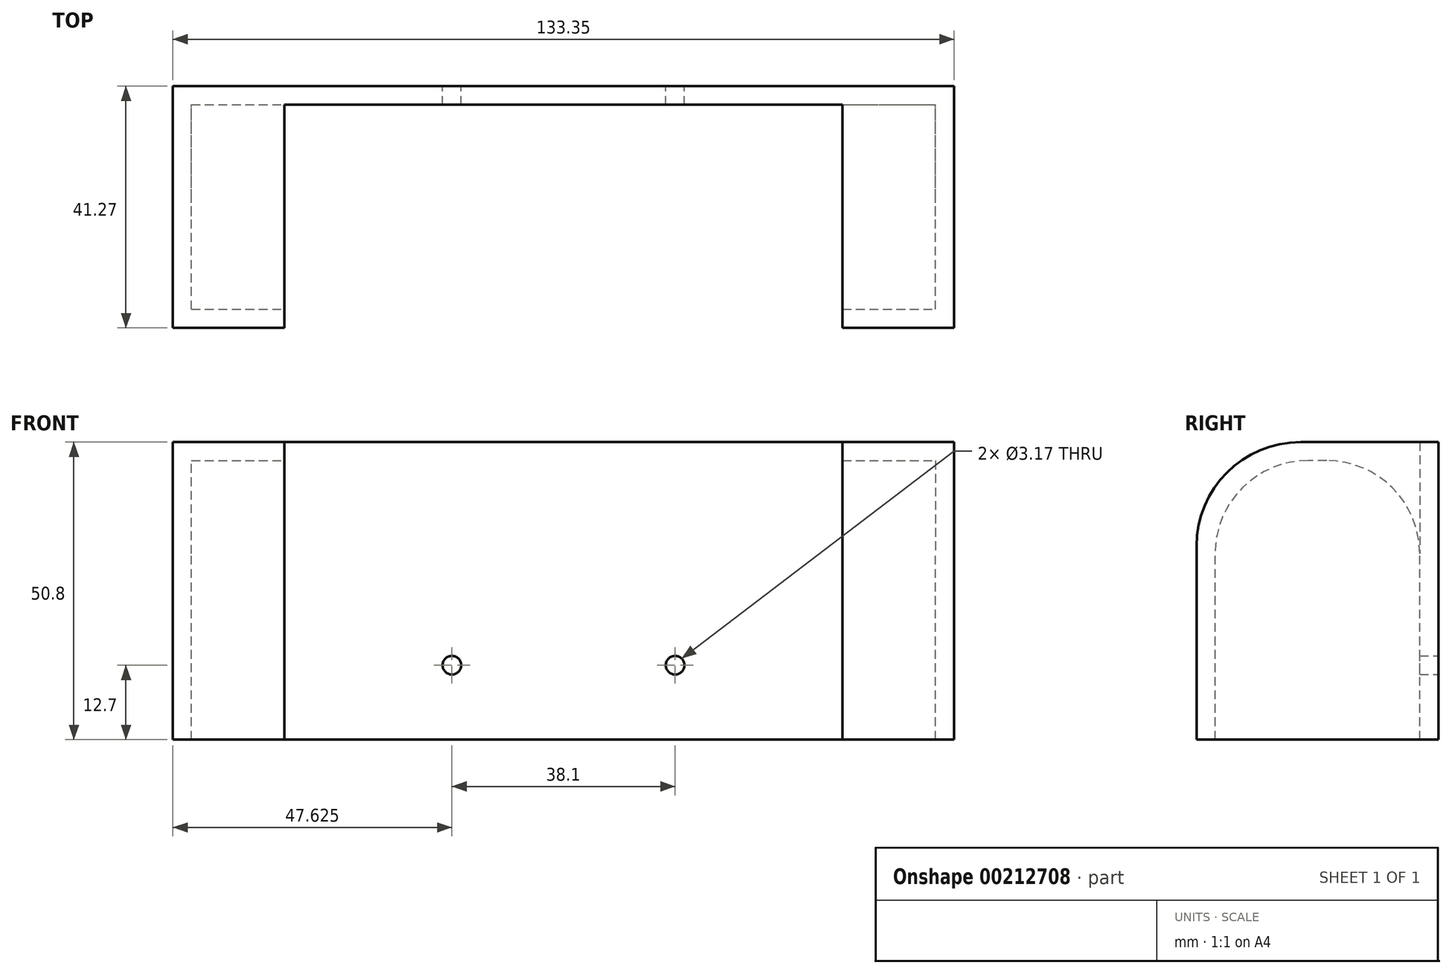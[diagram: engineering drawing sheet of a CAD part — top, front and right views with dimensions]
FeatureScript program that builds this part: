
annotation { "Feature Type Name" : "Feature", "Feature Type Description" : "" }
export const myFeature = defineFeature(function(context is Context, id is Id, definition is map)
    precondition{}
    {
        {
            var Q0;
            Q0=qCreatedBy(makeId("Front.planeOp"),FACE);
            var sketch = newSketch(context, id + "F0", { "sketchPlane" : qUnion([Q0])});
            skLineSegment(sketch, "E0.bottom", {"start": v(0, 0) * mm, "end": v(133.35, 0) * mm});
            skLineSegment(sketch, "E0.top", {"start": v(0, 50.8) * mm, "end": v(133.35, 50.8) * mm});
            skLineSegment(sketch, "E0.left", {"start": v(0, 0) * mm, "end": v(0, 50.8) * mm});
            skLineSegment(sketch, "E0.right", {"start": v(133.35, 0) * mm, "end": v(133.35, 50.8) * mm});
            skSolve(sketch);
        }
        {
            var Q0;
            Q0 = qSketchRegion(id + "F0", true);
            extrude(context, id + "F1", {"entities" : qUnion([Q0]), "depth" : 3.17 * mm});
        }
        {
            var Q0;
            Q0=makeQuery(id+"F1.opExtrude","CAP_FACE",FACE,{"disambiguationData":[OSD([sQuery(id+"F0.wireOp",EDGE,"E0.bottom"),sQuery(id+"F0.wireOp",EDGE,"E0.top"),sQuery(id+"F0.wireOp",EDGE,"E0.left"),sQuery(id+"F0.wireOp",EDGE,"E0.right")])],"isStart":false});
            var sketch = newSketch(context, id + "F2", { "sketchPlane" : qUnion([Q0])});
            skLineSegment(sketch, "E1.bottom", {"start": v(0, 50.8) * mm, "end": v(19.05, 50.8) * mm});
            skLineSegment(sketch, "E1.top", {"start": v(0, 0) * mm, "end": v(19.05, 0) * mm});
            skLineSegment(sketch, "E1.left", {"start": v(0, 50.8) * mm, "end": v(0, 0) * mm});
            skLineSegment(sketch, "E1.right", {"start": v(19.05, 50.8) * mm, "end": v(19.05, 0) * mm});
            skLineSegment(sketch, "E2.bottom", {"start": v(133.35, 50.8) * mm, "end": v(114.3, 50.8) * mm});
            skLineSegment(sketch, "E2.top", {"start": v(133.35, 0) * mm, "end": v(114.3, 0) * mm});
            skLineSegment(sketch, "E2.left", {"start": v(133.35, 50.8) * mm, "end": v(133.35, 0) * mm});
            skLineSegment(sketch, "E2.right", {"start": v(114.3, 50.8) * mm, "end": v(114.3, 0) * mm});
            skSolve(sketch);
        }
        {
            var Q0;
            Q0 = qSketchRegion(id + "F2", true);
            extrude(context, id + "F3", {"entities" : qUnion([Q0]), "operationType" : NewBodyOperationType.ADD, "depth" : 38.1 * mm});
        }
        {
            var Q0;
            Q0=makeQuery(id+"F3.boolean.opBoolean","MERGE",FACE,{"derivedFrom":[makeQuery(id+"F1.opExtrude","SWEPT_FACE",FACE,{"disambiguationData":[OSD([sQuery(id+"F0.wireOp",EDGE,"E0.bottom")])]}),makeQuery(id+"F3.opExtrude","SWEPT_FACE",FACE,{"disambiguationData":[OSD([sQuery(id+"F2.wireOp",EDGE,"E1.top")])]}),makeQuery(id+"F3.opExtrude","SWEPT_FACE",FACE,{"disambiguationData":[OSD([sQuery(id+"F2.wireOp",EDGE,"E2.top")])]})]});
            shell(context, id + "F4", {"entities" : qUnion([Q0]), "thickness" : 3.17 * mm});
        }
        {
            var Q0;
            Q0=makeQuery(id+"F4.opShell","OFFSET_EDGE",EDGE,{"disambiguationData":[OSD([sQuery(id+"F0.wireOp",EDGE,"E0.top")]),OD(0.0)]});
            var Q1;
            Q1=makeQuery(id+"F4.opShell","OFFSET_EDGE",EDGE,{"disambiguationData":[OSD([sQuery(id+"F2.wireOp",EDGE,"E1.bottom")])]});
            var Q2;
            Q2=makeQuery(id+"F4.opShell","OFFSET_EDGE",EDGE,{"disambiguationData":[OSD([sQuery(id+"F2.wireOp",EDGE,"E2.bottom")])]});
            var Q3;
            Q3=makeQuery(id+"F4.opShell","OFFSET_EDGE",EDGE,{"disambiguationData":[OSD([sQuery(id+"F0.wireOp",EDGE,"E0.top")]),OD(1.0)]});
            fillet(context, id + "F5", {"entities" : qUnion([Q0, Q1, Q2, Q3]), "radius" : 15.88 * mm, "tangentPropagation" : true, "allowEdgeOverflow" : false});
        }
        {
            var Q0;
            Q0=makeQuery(id+"F4.opShell","OFFSET_FACE",FACE,{"disambiguationData":[OSD([sQuery(id+"F2.wireOp",EDGE,"E1.right")])]});
            var sketch = newSketch(context, id + "F6", { "sketchPlane" : qUnion([Q0])});
            skSolve(sketch);
        }
        {
            var Q0;
            {var subQ0=sQuery(id+"F2.wireOp",EDGE,"E1.right");Q0=makeQuery(id+"F6.imprint","IMPRINT",FACE,{"disambiguationData":[TD([[makeQuery(id+"F6.imprint","IMPRINT",EDGE,{"derivedFrom":makeQuery(id+"F4.opShell","OFFSET_EDGE",EDGE,{"disambiguationData":[OSD([subQ0])]})}),-1.0]])]});}
            extrude(context, id + "F7", {"entities" : qUnion([Q0]), "operationType" : NewBodyOperationType.REMOVE, "oppositeDirection" : true, "depth" : 25.4 * mm});
        }
        {
            var Q0;
            Q0=makeQuery(id+"F4.opShell","OFFSET_FACE",FACE,{"disambiguationData":[OSD([sQuery(id+"F2.wireOp",EDGE,"E2.right")])]});
            extrude(context, id + "F8", {"entities" : qUnion([Q0]), "operationType" : NewBodyOperationType.REMOVE, "oppositeDirection" : true, "depth" : 25.4 * mm});
        }
        {
            var Q0;
            Q0=makeQuery(id+"F1.opExtrude","CAP_FACE",FACE,{"disambiguationData":[OSD([sQuery(id+"F0.wireOp",EDGE,"E0.bottom"),sQuery(id+"F0.wireOp",EDGE,"E0.top"),sQuery(id+"F0.wireOp",EDGE,"E0.left"),sQuery(id+"F0.wireOp",EDGE,"E0.right")])],"isStart":true});
            var sketch = newSketch(context, id + "F9", { "sketchPlane" : qUnion([Q0])});
            skLineSegment(sketch, "E3", {"start": v(0, 12.7) * mm, "end": v(-133.35, 12.7) * mm, "construction": true});
            skLineSegment(sketch, "E4", {"start": v(-66.68, 0) * mm, "end": v(-66.68, 50.8) * mm, "construction": true});
            skCircle(sketch, "E5", {"center": v(-47.63, 12.7) * mm, "radius": 1.59 * mm});
            skCircle(sketch, "E6", {"center": v(-85.73, 12.7) * mm, "radius": 1.59 * mm});
            skSolve(sketch);
        }
        {
            var Q0;
            Q0 = qSketchRegion(id + "F9", true);
            extrude(context, id + "F10", {"entities" : qUnion([Q0]), "operationType" : NewBodyOperationType.REMOVE, "oppositeDirection" : true, "depth" : 25.4 * mm});
        }
        {
            var Q0;
            Q0=makeQuery(id+"F3.opExtrude","CAP_EDGE",EDGE,{"disambiguationData":[OSD([sQuery(id+"F2.wireOp",EDGE,"E1.bottom")])],"isStart":false});
            var Q1;
            Q1=makeQuery(id+"F3.opExtrude","CAP_EDGE",EDGE,{"disambiguationData":[OSD([sQuery(id+"F2.wireOp",EDGE,"E2.bottom")])],"isStart":false});
            fillet(context, id + "F11", {"entities" : qUnion([Q0, Q1]), "radius" : 17.78 * mm, "tangentPropagation" : true, "allowEdgeOverflow" : false});
        }
    });
